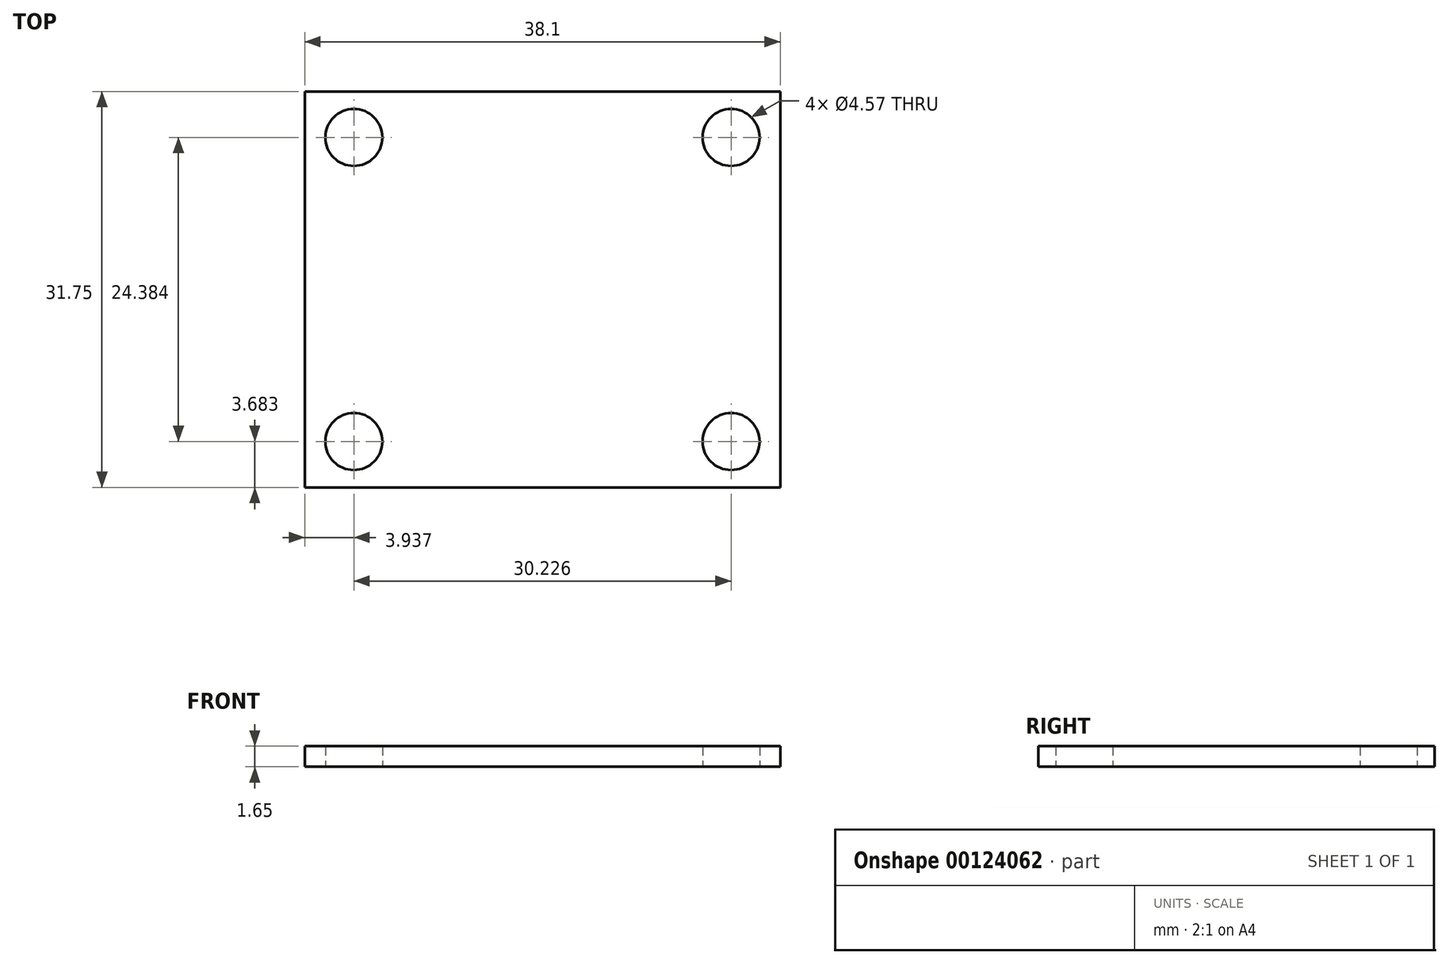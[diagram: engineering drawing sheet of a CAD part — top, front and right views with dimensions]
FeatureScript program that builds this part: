
annotation { "Feature Type Name" : "Feature", "Feature Type Description" : "" }
export const myFeature = defineFeature(function(context is Context, id is Id, definition is map)
    precondition{}
    {
        {
            var Q0;
            Q0=qCreatedBy(makeId("Top.planeOp"),FACE);
            var sketch = newSketch(context, id + "F0", { "sketchPlane" : qUnion([Q0])});
            skLineSegment(sketch, "E0.bottom", {"start": v(0, 0) * mm, "end": v(38.1, 0) * mm});
            skLineSegment(sketch, "E0.top", {"start": v(0, 31.75) * mm, "end": v(38.1, 31.75) * mm});
            skLineSegment(sketch, "E0.left", {"start": v(0, 0) * mm, "end": v(0, 31.75) * mm});
            skLineSegment(sketch, "E0.right", {"start": v(38.1, 0) * mm, "end": v(38.1, 31.75) * mm});
            skCircle(sketch, "E1", {"center": v(3.94, 28.07) * mm, "radius": 2.29 * mm});
            skCircle(sketch, "E2", {"center": v(3.94, 3.68) * mm, "radius": 2.29 * mm});
            skCircle(sketch, "E3", {"center": v(34.16, 3.68) * mm, "radius": 2.29 * mm});
            skCircle(sketch, "E4", {"center": v(34.16, 28.07) * mm, "radius": 2.29 * mm});
            skSolve(sketch);
        }
        {
            var Q0;
            Q0=makeQuery(id+"F0.imprint","IMPRINT",FACE,{"disambiguationData":[TD([[makeQuery(id+"F0.imprint","IMPRINT",EDGE,{"derivedFrom":sQuery(id+"F0.wireOp",EDGE,"E0.bottom")}),1.0]])]});
            extrude(context, id + "F1", {"entities" : qUnion([Q0]), "depth" : 1.65 * mm});
        }
    });
